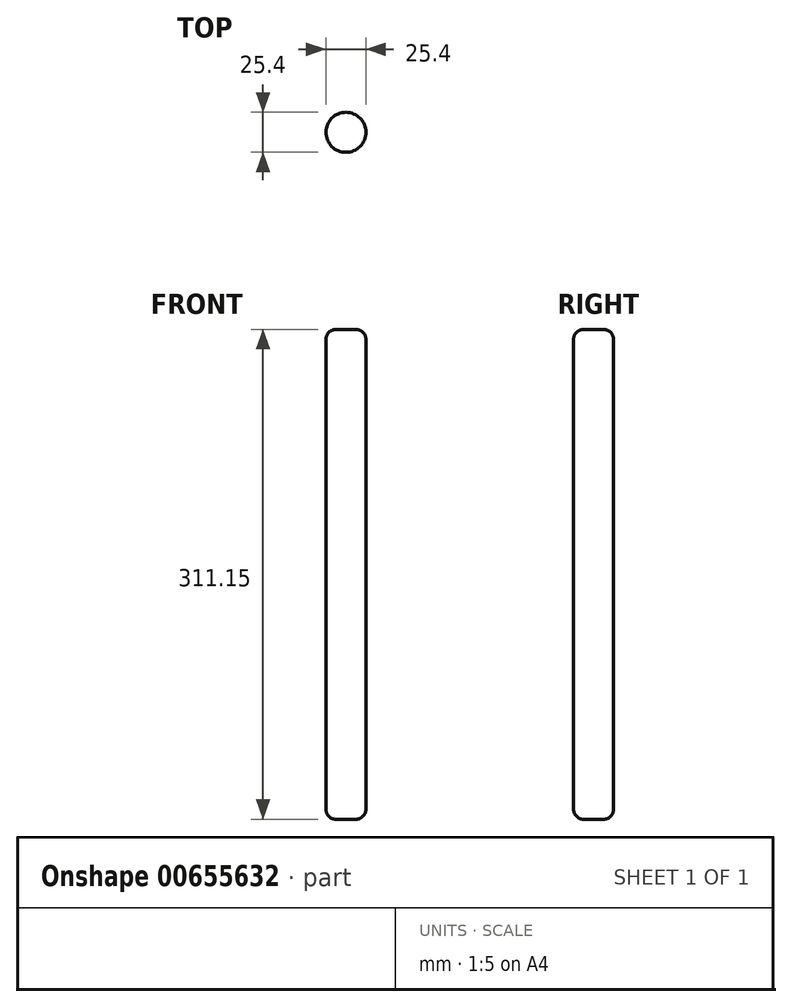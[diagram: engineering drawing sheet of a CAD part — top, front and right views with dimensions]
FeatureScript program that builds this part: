
annotation { "Feature Type Name" : "Feature", "Feature Type Description" : "" }
export const myFeature = defineFeature(function(context is Context, id is Id, definition is map)
    precondition{}
    {
        {
            var Q0;
            Q0=qCreatedBy(makeId("Top.planeOp"),FACE);
            var sketch = newSketch(context, id + "F0", { "sketchPlane" : qUnion([Q0])});
            skCircle(sketch, "E0", {"center": v(0, 0) * mm, "radius": 12.7 * mm});
            skSolve(sketch);
        }
        {
            var Q0;
            Q0=makeQuery(id+"F0.imprint","IMPRINT",FACE,{"disambiguationData":[TD([[makeQuery(id+"F0.imprint","IMPRINT",EDGE,{"derivedFrom":sQuery(id+"F0.wireOp",EDGE,"E0")}),1.0]])]});
            extrude(context, id + "F1", {"entities" : qUnion([Q0]), "depth" : 311.15 * mm, "offsetDistance" : 25.4 * mm});
        }
        {
            var Q0;
            Q0=makeQuery(id+"F1.opExtrude","SWEPT_FACE",FACE,{"disambiguationData":[OSD([sQuery(id+"F0.wireOp",EDGE,"E0")])]});
            var Q1;
            Q1=makeQuery(id+"F1.opExtrude","CAP_EDGE",EDGE,{"disambiguationData":[OSD([sQuery(id+"F0.wireOp",EDGE,"E0")])],"isStart":false});
            fillet(context, id + "F2", {"entities" : qUnion([Q0, Q1]), "radius" : 6.35 * mm, "tangentPropagation" : true, "allowEdgeOverflow" : false});
        }
    });
